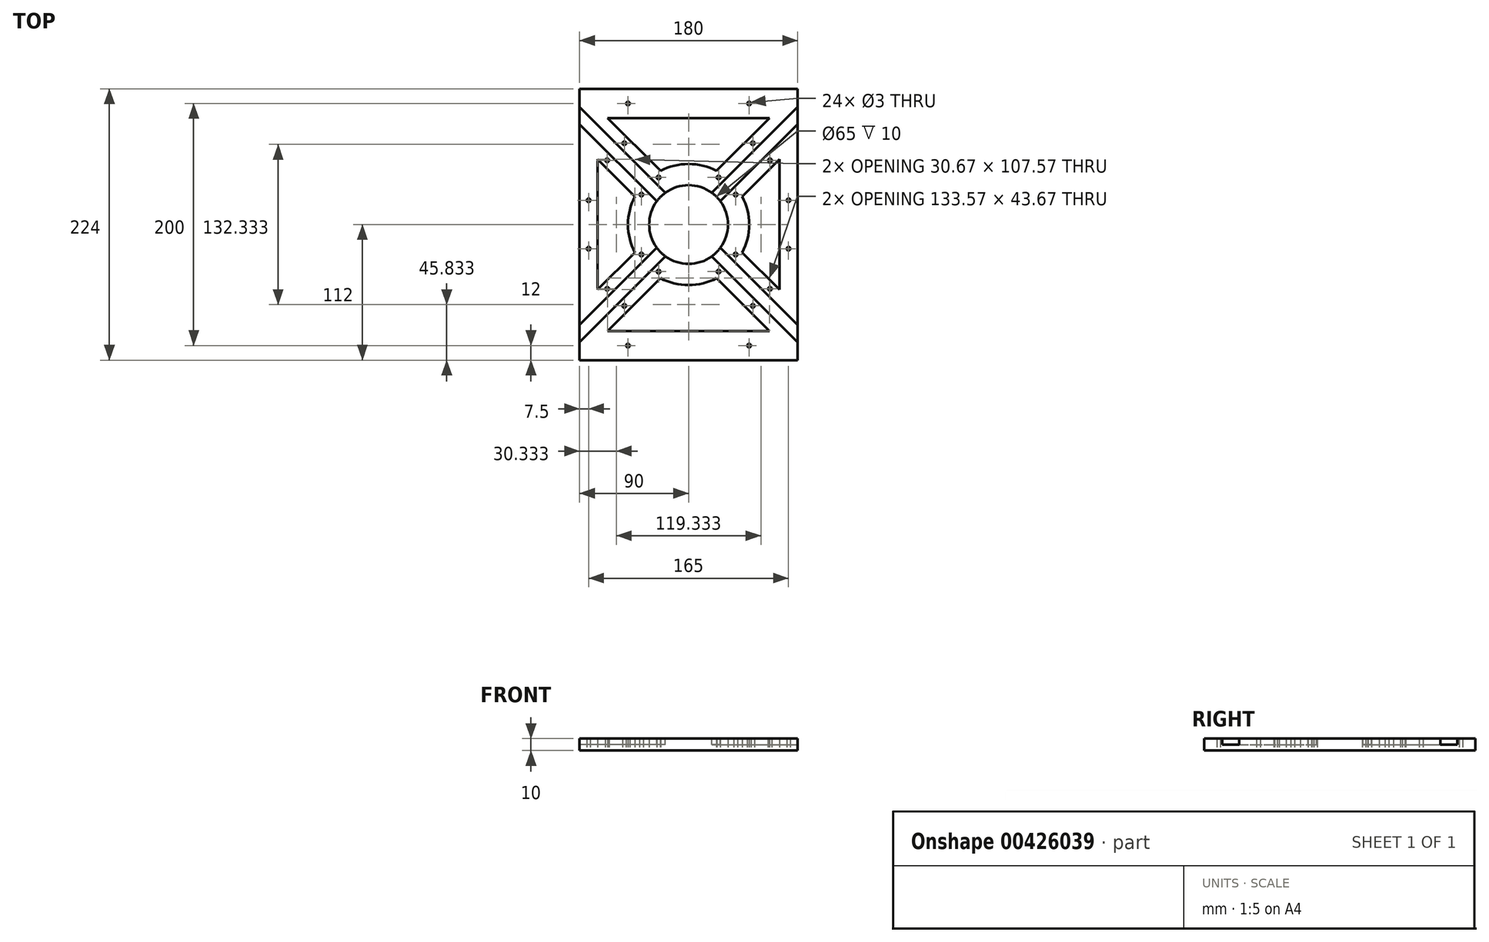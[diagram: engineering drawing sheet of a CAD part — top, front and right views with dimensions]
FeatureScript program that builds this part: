
annotation { "Feature Type Name" : "Feature", "Feature Type Description" : "" }
export const myFeature = defineFeature(function(context is Context, id is Id, definition is map)
    precondition{}
    {
        {
            var Q0;
            Q0=qCreatedBy(makeId("Top.planeOp"),FACE);
            var sketch = newSketch(context, id + "F0", { "sketchPlane" : qUnion([Q0])});
            skLineSegment(sketch, "E0.bottom", {"start": v(90, -112) * mm, "end": v(-90, -112) * mm});
            skLineSegment(sketch, "E0.top", {"start": v(90, 112) * mm, "end": v(-90, 112) * mm});
            skLineSegment(sketch, "E0.left", {"start": v(90, -112) * mm, "end": v(90, 112) * mm});
            skLineSegment(sketch, "E0.right", {"start": v(-90, -112) * mm, "end": v(-90, 112) * mm});
            skPoint(sketch, "E0.middle", {"position": v(0, 0) * mm});
            skCircle(sketch, "E1", {"center": v(0, 0) * mm, "radius": 32.5 * mm});
            skLineSegment(sketch, "E2.bottom", {"start": v(75, -75) * mm, "end": v(-75, -75) * mm, "construction": true});
            skLineSegment(sketch, "E2.top", {"start": v(75, 75) * mm, "end": v(75, 75) * mm});
            skLineSegment(sketch, "E2.left", {"start": v(75, -75) * mm, "end": v(75, 75) * mm});
            skLineSegment(sketch, "E2.right", {"start": v(-75, -75) * mm, "end": v(-75, -75) * mm});
            skPoint(sketch, "E3", {"position": v(0, 75) * mm});
            skPoint(sketch, "E4", {"position": v(-75, 0) * mm});
            skLineSegment(sketch, "E5", {"start": v(75, 75) * mm, "end": v(-75, 75) * mm, "construction": true});
            skLineSegment(sketch, "E6", {"start": v(-75, -75) * mm, "end": v(-75, 75) * mm});
            skArc(sketch, "E7", {"start": v(0, 50) * mm, "mid": v(-35.36, 35.36) * mm, "end": v(-50, 0) * mm});
            skArc(sketch, "E8", {"start": v(-50, 0) * mm, "mid": v(-35.36, -35.36) * mm, "end": v(0, -50) * mm});
            skArc(sketch, "E9", {"start": v(0, -50) * mm, "mid": v(35.36, -35.36) * mm, "end": v(50, 0) * mm});
            skArc(sketch, "E10", {"start": v(50, 0) * mm, "mid": v(46.2, 19.13) * mm, "end": v(35.36, 35.36) * mm});
            skArc(sketch, "E11", {"start": v(35.36, 35.36) * mm, "mid": v(19.13, 46.2) * mm, "end": v(0, 50) * mm});
            skCircle(sketch, "E12", {"center": v(-50, 100) * mm, "radius": 1.5 * mm});
            skCircle(sketch, "E13.MirrorC", {"center": v(50, 100) * mm, "radius": 1.5 * mm});
            skCircle(sketch, "E14.MirrorC", {"center": v(-50, -100) * mm, "radius": 1.5 * mm});
            skCircle(sketch, "E15.MirrorC", {"center": v(50, -100) * mm, "radius": 1.5 * mm});
            skLineSegment(sketch, "E16", {"start": v(-75, -75) * mm, "end": v(75, 75) * mm, "construction": true});
            skLineSegment(sketch, "E17", {"start": v(-75, 75) * mm, "end": v(75, -75) * mm, "construction": true});
            skLineSegment(sketch, "E18", {"start": v(-53.79, 75) * mm, "end": v(-23.12, 44.33) * mm});
            skLineSegment(sketch, "E19.MirrorCS", {"start": v(-75, 53.79) * mm, "end": v(-44.33, 23.12) * mm});
            skLineSegment(sketch, "E20.MirrorCS", {"start": v(75, -53.79) * mm, "end": v(44.33, -23.12) * mm});
            skLineSegment(sketch, "E21.MirrorCS", {"start": v(53.79, -75) * mm, "end": v(23.12, -44.33) * mm});
            skLineSegment(sketch, "E22.MirrorCS", {"start": v(53.79, 75) * mm, "end": v(23.12, 44.33) * mm});
            skLineSegment(sketch, "E23.MirrorCS", {"start": v(75, 53.79) * mm, "end": v(44.33, 23.12) * mm});
            skLineSegment(sketch, "E24.MirrorCS", {"start": v(-66.79, -88) * mm, "end": v(-23.12, -44.33) * mm});
            skLineSegment(sketch, "E25.MirrorCS", {"start": v(-75, -53.79) * mm, "end": v(-44.33, -23.12) * mm});
            skCircle(sketch, "E26", {"center": v(-53.03, 67.18) * mm, "radius": 1.5 * mm});
            skCircle(sketch, "E27", {"center": v(-24.75, 38.9) * mm, "radius": 1.5 * mm});
            skCircle(sketch, "E28.MirrorC", {"center": v(-67.18, 53.03) * mm, "radius": 1.5 * mm});
            skCircle(sketch, "E29.MirrorC", {"center": v(-38.9, 24.75) * mm, "radius": 1.5 * mm});
            skCircle(sketch, "E30.MirrorC", {"center": v(38.9, -24.75) * mm, "radius": 1.5 * mm});
            skCircle(sketch, "E31.MirrorC", {"center": v(24.75, -38.9) * mm, "radius": 1.5 * mm});
            skCircle(sketch, "E32.MirrorC", {"center": v(53.03, -67.18) * mm, "radius": 1.5 * mm});
            skCircle(sketch, "E33.MirrorC", {"center": v(67.18, -53.03) * mm, "radius": 1.5 * mm});
            skCircle(sketch, "E34.MirrorC", {"center": v(24.75, 38.9) * mm, "radius": 1.5 * mm});
            skCircle(sketch, "E35.MirrorC", {"center": v(38.9, 24.75) * mm, "radius": 1.5 * mm});
            skCircle(sketch, "E36.MirrorC", {"center": v(67.18, 53.03) * mm, "radius": 1.5 * mm});
            skCircle(sketch, "E37.MirrorC", {"center": v(53.03, 67.18) * mm, "radius": 1.5 * mm});
            skCircle(sketch, "E38.MirrorC", {"center": v(-24.75, -38.9) * mm, "radius": 1.5 * mm});
            skCircle(sketch, "E39.MirrorC", {"center": v(-38.9, -24.75) * mm, "radius": 1.5 * mm});
            skCircle(sketch, "E40.MirrorC", {"center": v(-67.18, -53.03) * mm, "radius": 1.5 * mm});
            skCircle(sketch, "E41.MirrorC", {"center": v(-53.03, -67.18) * mm, "radius": 1.5 * mm});
            skCircle(sketch, "E42", {"center": v(-82.5, 20) * mm, "radius": 1.5 * mm});
            skCircle(sketch, "E43.MirrorC", {"center": v(-82.5, -20) * mm, "radius": 1.5 * mm});
            skCircle(sketch, "E44.MirrorC", {"center": v(82.5, 20) * mm, "radius": 1.5 * mm});
            skCircle(sketch, "E45.MirrorC", {"center": v(82.5, -20) * mm, "radius": 1.5 * mm});
            skLineSegment(sketch, "E46.bottom", {"start": v(-75, 75) * mm, "end": v(75, 75) * mm, "construction": true});
            skLineSegment(sketch, "E46.top", {"start": v(-75, 88) * mm, "end": v(75, 88) * mm});
            skLineSegment(sketch, "E46.left", {"start": v(-75, 75) * mm, "end": v(-75, 88) * mm});
            skLineSegment(sketch, "E46.right", {"start": v(75, 75) * mm, "end": v(75, 88) * mm});
            skLineSegment(sketch, "E47.MirrorCS", {"start": v(-75, -88) * mm, "end": v(75, -88) * mm});
            skLineSegment(sketch, "E48.MirrorCS", {"start": v(75, -75) * mm, "end": v(75, -88) * mm});
            skLineSegment(sketch, "E49.MirrorCS", {"start": v(-75, -75) * mm, "end": v(-75, -88) * mm});
            skPoint(sketch, "E50.orphan", {"position": v(-53.79, -75) * mm});
            skLineSegment(sketch, "E51.MirrorCS", {"start": v(66.79, -88) * mm, "end": v(23.12, -44.33) * mm});
            skLineSegment(sketch, "E52.MirrorCS", {"start": v(-66.79, 88) * mm, "end": v(-23.12, 44.33) * mm});
            skLineSegment(sketch, "E53.MirrorCS", {"start": v(66.79, 88) * mm, "end": v(23.12, 44.33) * mm});
            skSolve(sketch);
        }
        {
            var Q0;
            Q0=makeQuery(id+"F0.imprint","IMPRINT",FACE,{"disambiguationData":[TD([[makeQuery(id+"F0.imprint","IMPRINT",EDGE,{"derivedFrom":sQuery(id+"F0.wireOp",EDGE,"E0.bottom")}),-1.0]])]});
            var Q1;
            {var subQ1=sQuery(id+"F0.wireOp",EDGE,"E18");Q1=makeQuery(id+"F0.imprint","IMPRINT",FACE,{"disambiguationData":[TD([[makeQuery(id+"F0.imprint","IMPRINT",EDGE,{"derivedFrom":subQ1}),-1.0]])]});}
            var Q2;
            Q2=makeQuery(id+"F0.imprint","IMPRINT",FACE,{"disambiguationData":[TD([[makeQuery(id+"F0.imprint","IMPRINT",EDGE,{"derivedFrom":sQuery(id+"F0.wireOp",EDGE,"E1")}),-1.0]])]});
            var Q3;
            {var subQ4=sQuery(id+"F0.wireOp",EDGE,"E22.MirrorCS");Q3=makeQuery(id+"F0.imprint","IMPRINT",FACE,{"disambiguationData":[TD([[makeQuery(id+"F0.imprint","IMPRINT",EDGE,{"derivedFrom":subQ4}),1.0]])]});}
            var Q4;
            {var subQ1=sQuery(id+"F0.wireOp",EDGE,"E20.MirrorCS");Q4=makeQuery(id+"F0.imprint","IMPRINT",FACE,{"disambiguationData":[TD([[makeQuery(id+"F0.imprint","IMPRINT",EDGE,{"derivedFrom":subQ1}),1.0]])]});}
            var Q5;
            {var subQ0=sQuery(id+"F0.wireOp",EDGE,"E24.MirrorCS");Q5=makeQuery(id+"F0.imprint","IMPRINT",FACE,{"disambiguationData":[TD([[makeQuery(id+"F0.imprint","IMPRINT",EDGE,{"derivedFrom":subQ0}),1.0]])]});}
            var Q6;
            {var subQ4=sQuery(id+"F0.wireOp",EDGE,"E19.MirrorCS");Q6=makeQuery(id+"F0.imprint","IMPRINT",FACE,{"disambiguationData":[TD([[makeQuery(id+"F0.imprint","IMPRINT",EDGE,{"derivedFrom":subQ4}),1.0]])]});}
            var Q7;
            {var subQ0=sQuery(id+"F0.wireOp",EDGE,"E23.MirrorCS");Q7=makeQuery(id+"F0.imprint","IMPRINT",FACE,{"disambiguationData":[TD([[makeQuery(id+"F0.imprint","IMPRINT",EDGE,{"derivedFrom":subQ0}),-1.0]])]});}
            extrude(context, id + "F1", {"entities" : qUnion([Q0, Q1, Q2, Q3, Q4, Q5, Q6, Q7]), "depth" : 10 * mm});
        }
        {
            var Q0;
            Q0=makeQuery(id+"F1.opExtrude","CAP_FACE",FACE,{"disambiguationData":[OSD([sQuery(id+"F0.wireOp",EDGE,"E0.bottom"),sQuery(id+"F0.wireOp",EDGE,"E0.top"),sQuery(id+"F0.wireOp",EDGE,"E0.left"),sQuery(id+"F0.wireOp",EDGE,"E0.right"),sQuery(id+"F0.wireOp",EDGE,"E1"),sQuery(id+"F0.wireOp",EDGE,"E2.left"),sQuery(id+"F0.wireOp",EDGE,"E6"),sQuery(id+"F0.wireOp",EDGE,"E7"),sQuery(id+"F0.wireOp",EDGE,"E8"),sQuery(id+"F0.wireOp",EDGE,"E9"),sQuery(id+"F0.wireOp",EDGE,"E10"),sQuery(id+"F0.wireOp",EDGE,"E11"),sQuery(id+"F0.wireOp",EDGE,"E12"),sQuery(id+"F0.wireOp",EDGE,"E13.MirrorC"),sQuery(id+"F0.wireOp",EDGE,"E14.MirrorC"),sQuery(id+"F0.wireOp",EDGE,"E15.MirrorC"),sQuery(id+"F0.wireOp",EDGE,"E19.MirrorCS"),sQuery(id+"F0.wireOp",EDGE,"E20.MirrorCS"),sQuery(id+"F0.wireOp",EDGE,"E23.MirrorCS"),sQuery(id+"F0.wireOp",EDGE,"E24.MirrorCS"),sQuery(id+"F0.wireOp",EDGE,"E25.MirrorCS"),sQuery(id+"F0.wireOp",EDGE,"E26"),sQuery(id+"F0.wireOp",EDGE,"E27"),sQuery(id+"F0.wireOp",EDGE,"E28.MirrorC"),sQuery(id+"F0.wireOp",EDGE,"E29.MirrorC"),sQuery(id+"F0.wireOp",EDGE,"E30.MirrorC"),sQuery(id+"F0.wireOp",EDGE,"E31.MirrorC"),sQuery(id+"F0.wireOp",EDGE,"E32.MirrorC"),sQuery(id+"F0.wireOp",EDGE,"E33.MirrorC"),sQuery(id+"F0.wireOp",EDGE,"E34.MirrorC"),sQuery(id+"F0.wireOp",EDGE,"E35.MirrorC"),sQuery(id+"F0.wireOp",EDGE,"E36.MirrorC"),sQuery(id+"F0.wireOp",EDGE,"E37.MirrorC"),sQuery(id+"F0.wireOp",EDGE,"E38.MirrorC"),sQuery(id+"F0.wireOp",EDGE,"E39.MirrorC"),sQuery(id+"F0.wireOp",EDGE,"E40.MirrorC"),sQuery(id+"F0.wireOp",EDGE,"E41.MirrorC"),sQuery(id+"F0.wireOp",EDGE,"E42"),sQuery(id+"F0.wireOp",EDGE,"E43.MirrorC"),sQuery(id+"F0.wireOp",EDGE,"E44.MirrorC"),sQuery(id+"F0.wireOp",EDGE,"E45.MirrorC"),sQuery(id+"F0.wireOp",EDGE,"E46.top"),sQuery(id+"F0.wireOp",EDGE,"E47.MirrorCS"),sQuery(id+"F0.wireOp",EDGE,"E51.MirrorCS"),sQuery(id+"F0.wireOp",EDGE,"E52.MirrorCS"),sQuery(id+"F0.wireOp",EDGE,"E53.MirrorCS")])],"isStart":false});
            var sketch = newSketch(context, id + "F2", { "sketchPlane" : qUnion([Q0])});
            skLineSegment(sketch, "E54.bottom", {"start": v(75, -75) * mm, "end": v(-75, -75) * mm, "construction": true});
            skLineSegment(sketch, "E54.top", {"start": v(75, 75) * mm, "end": v(-75, 75) * mm, "construction": true});
            skLineSegment(sketch, "E54.left", {"start": v(75, -75) * mm, "end": v(75, 75) * mm, "construction": true});
            skLineSegment(sketch, "E54.right", {"start": v(-75, -75) * mm, "end": v(-75, 75) * mm, "construction": true});
            skPoint(sketch, "E54.middle", {"position": v(0, 0) * mm});
            skLineSegment(sketch, "E55", {"start": v(-75, 75) * mm, "end": v(75, -75) * mm, "construction": true});
            skLineSegment(sketch, "E56", {"start": v(-75, -75) * mm, "end": v(75, 75) * mm, "construction": true});
            skLineSegment(sketch, "E57", {"start": v(-105.4, -98.34) * mm, "end": v(104.93, 112) * mm});
            skLineSegment(sketch, "E58.MirrorCS", {"start": v(-98.64, -105.71) * mm, "end": v(112, 104.93) * mm});
            skPoint(sketch, "E59.orphan", {"position": v(-82.93, -90) * mm});
            skPoint(sketch, "E60.orphan", {"position": v(-90, -82.93) * mm});
            skLineSegment(sketch, "E61.MirrorCS", {"start": v(105.4, -98.34) * mm, "end": v(-104.93, 112) * mm});
            skLineSegment(sketch, "E62.MirrorCS", {"start": v(98.64, -105.71) * mm, "end": v(-112, 104.93) * mm});
            skLineSegment(sketch, "E63", {"start": v(-112, 104.93) * mm, "end": v(-104.93, 112) * mm});
            skLineSegment(sketch, "E64", {"start": v(98.64, -105.71) * mm, "end": v(105.4, -98.34) * mm});
            skLineSegment(sketch, "E65", {"start": v(-105.4, -98.34) * mm, "end": v(-98.64, -105.71) * mm});
            skLineSegment(sketch, "E66", {"start": v(104.93, 112) * mm, "end": v(112, 104.93) * mm});
            skSolve(sketch);
        }
        {
            var Q0;
            {var subQ0=sQuery(id+"F2.wireOp",EDGE,"E61.MirrorCS");var subQ1=makeQuery(id+"F1.opExtrude","CAP_EDGE",EDGE,{"disambiguationData":[OSD([sQuery(id+"F0.wireOp",EDGE,"E0.right")])],"isStart":false});var subQ2=makeQuery(id+"F2.imprint","INTERSECT",VERTEX,{"derivedFrom":[subQ1,subQ0]});Q0=makeQuery(id+"F2.imprint","IMPRINT",FACE,{"disambiguationData":[TD([[makeQuery(id+"F2.imprint","IMPRINT",EDGE,{"disambiguationData":[TD([[subQ2,1.0]])],"derivedFrom":subQ0}),1.0]])]});}
            var Q1;
            {var subQ0=sQuery(id+"F2.wireOp",EDGE,"E57");var subQ1=makeQuery(id+"F1.opExtrude","CAP_EDGE",EDGE,{"disambiguationData":[OSD([sQuery(id+"F0.wireOp",EDGE,"E0.left")])],"isStart":false});var subQ2=makeQuery(id+"F2.imprint","INTERSECT",VERTEX,{"derivedFrom":[subQ1,subQ0]});Q1=makeQuery(id+"F2.imprint","IMPRINT",FACE,{"disambiguationData":[TD([[makeQuery(id+"F2.imprint","IMPRINT",EDGE,{"disambiguationData":[TD([[subQ2,1.0]])],"derivedFrom":subQ0}),-1.0]])]});}
            var Q2;
            {var subQ0=sQuery(id+"F2.wireOp",EDGE,"E61.MirrorCS");var subQ1=makeQuery(id+"F1.opExtrude","CAP_EDGE",EDGE,{"disambiguationData":[OSD([sQuery(id+"F0.wireOp",EDGE,"E0.left")])],"isStart":false});var subQ2=makeQuery(id+"F2.imprint","INTERSECT",VERTEX,{"derivedFrom":[subQ1,subQ0]});Q2=makeQuery(id+"F2.imprint","IMPRINT",FACE,{"disambiguationData":[TD([[makeQuery(id+"F2.imprint","IMPRINT",EDGE,{"disambiguationData":[TD([[subQ2,-1.0]])],"derivedFrom":subQ0}),1.0]])]});}
            var Q3;
            {var subQ0=sQuery(id+"F2.wireOp",EDGE,"E57");var subQ1=makeQuery(id+"F1.opExtrude","CAP_EDGE",EDGE,{"disambiguationData":[OSD([sQuery(id+"F0.wireOp",EDGE,"E0.right")])],"isStart":false});var subQ2=makeQuery(id+"F2.imprint","INTERSECT",VERTEX,{"derivedFrom":[subQ1,subQ0]});Q3=makeQuery(id+"F2.imprint","IMPRINT",FACE,{"disambiguationData":[TD([[makeQuery(id+"F2.imprint","IMPRINT",EDGE,{"disambiguationData":[TD([[subQ2,-1.0]])],"derivedFrom":subQ0}),-1.0]])]});}
            extrude(context, id + "F3", {"entities" : qUnion([Q0, Q1, Q2, Q3]), "operationType" : NewBodyOperationType.REMOVE, "oppositeDirection" : true, "depth" : 5 * mm});
        }
    });
